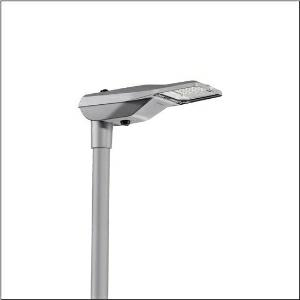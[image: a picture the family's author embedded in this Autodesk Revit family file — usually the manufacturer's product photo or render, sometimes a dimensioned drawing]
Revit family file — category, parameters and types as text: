
# Revit family: streetlight_sl_21_iq_micro___p0_5a_5xe1v31y08db_c8d5
name_source: partatom
category: Lighting Fixtures
units: mm (PartAtom-declared; Revit-internal decimal feet)

## family parameters
Cut with Voids When Loaded = No
Host = Face
Light Source = No
Part Type = Normal
Room Calculation Point = No
Round Connector Dimension = Use Diameter
Shared = No

## types (1)
- --- (1 x LED, 5030 lm, 39.1 W, 3000K)
    Apparent Load = 39 VA
    CIE Flux Codes = 37 73 96 100 100
    Color Rendering = 70
    Color Temperature = 3000K
    Default Elevation = 1800 mm
    Description = Streetlight SL 21 iQ micro, mast luminaire, primary light control with lens, of PMMA, primary optical cover: cover, of toughened safety glass, transparent, light distribution: P0.5a, light emission: direct distribution, primary light characteristic: asymmetric, installation type: post-top, side-entry, LED, High Power LED, rated luminous flux: 5.030lm, luminous efficacy: 129lm/W, light colour: 730, colour temperature: 3000K, control gear: iQ-Street Remote, D4i with power reduction, control: pre-setting: logarithmic dimming characteristic, Street-Remote, Auto-Match, Temp-Guard, Lumen-Switch, Night-Set, Smart-Wire, Light-Fading, Desk-Remote (wireless, voltage-free reading and setting of iQ features in the workshop via application-optimized NFC function/RFID function), optimised constant luminous flux control (CLO 2.0), mains connection: 220..240V, AC, 50/60Hz, start of lifetime: 39W, end of service life: 41W, reduction: 17W, luminaire housing, of diecast aluminium, powder-coated, SITECO metallic grey (DB 702S), corrosivity category C5 high according to DIN EN ISO 12944, please order mast flange separately, inclination adjustable: 0°, 5°, 10°, 15°, sealing non-destructively replaceable, multi-level sealing system, length: 528mm, width: 235mm, height: 110mm, mast flange for spigot size: 42mm (side-entry): 5XC10008XM4, 60/48mm (side-entry/post-top): 5XC10108XM2, 76/60mm (side-entry/post-top): 5XC10108XM1, mounting height: 4..8m, Smart Interface below and above, protection rating (complete): IP66, insulation class (complete): insulation class II (safety insulation), certification: CE, ENEC, ENEC+, VDE, impact resistance: IK10, permissible operating ambient temperature for outdoor applications: -40..+50°C, standard-compliant lighting for roads and squares, packaging unit: 1 piece

Light Distribution: P0.5a
    Height = 110 mm
    Lamp = 1 x LED
    Lamp Light Flux = 5030 lm
    Lamp Power = 39.1 W
    Lamp count = 1
    Length = 528 mm
    Luminous efficacy = 129 lm/W
    Manufacturer = Siteco
    ModVariant = No
    Model = 5XE1V31Y08DB
    Number of Poles = 1
    OnlyDefault = Yes
    Power Factor = 1
    Product Name = Streetlight SL 21 iQ micro | P0.5a
    Product group = mast luminaire | pylon top
    ProductGroupID = 6100
    Protection Class = Protection class II
    Protection Degree = IP 66
    RLX_Detail_Level = 1
    RLX_Emergency_Light_Flux = 0 lm
    RLX_Emergency_Type = 0
    RLX_Emergency_Type_DB = No
    RlxData = <blob elided: 98785 chars, md5=60d5f3d7>
    Socket = socket
    Standby Power = 0 W
    System Light Flux = 5030 lm
    System Power = 39 W
    Type Comments = factory setting: luminous flux: 100 % | dim-lin: 254 | 765 mA
    Type Image = l_1007239.jpg
    URL = http://relux.com
    VarID = @adj_078531
    Voltage = 0 V
    Weight = 0.00 kg
    Width = 235 mm

## geometry (parser evidence)
native form markers: Blend x4, Sweep x10
no freeform markers — native parametric forms only
